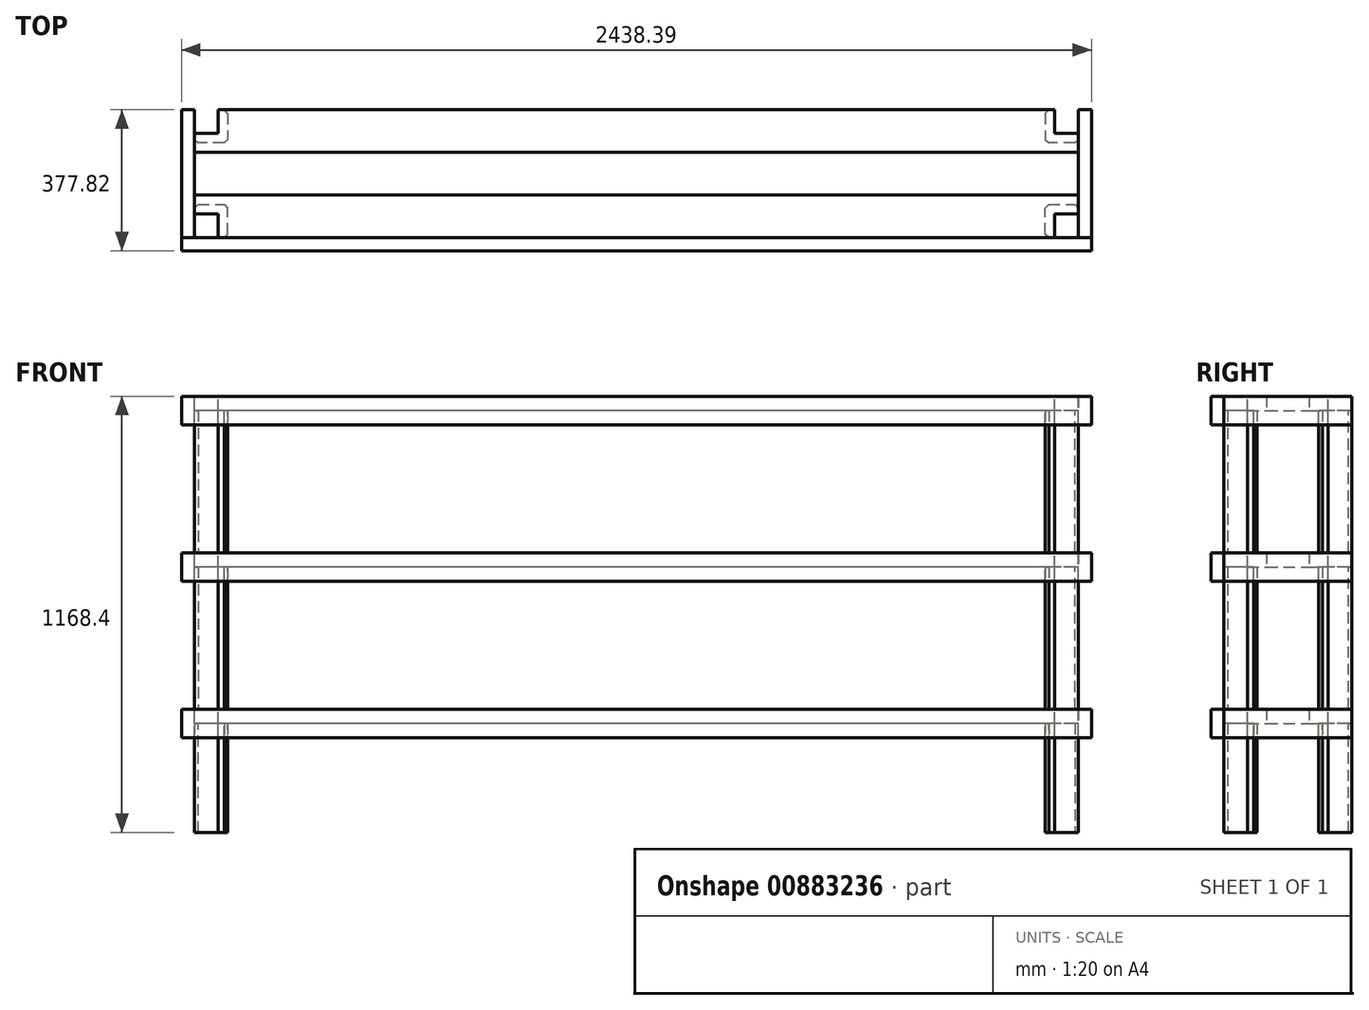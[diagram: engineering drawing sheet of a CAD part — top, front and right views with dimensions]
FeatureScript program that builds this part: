
annotation { "Feature Type Name" : "Feature", "Feature Type Description" : "" }
export const myFeature = defineFeature(function(context is Context, id is Id, definition is map)
    precondition{}
    {
        {
            var Q0;
            Q0=qCreatedBy(makeId("Top.planeOp"),FACE);
            var sketch = newSketch(context, id + "F0", { "sketchPlane" : qUnion([Q0])});
            skLineSegment(sketch, "E0.bottom", {"start": v(0, 0) * mm, "end": v(88.9, 0) * mm});
            skLineSegment(sketch, "E0.top", {"start": v(0, 88.9) * mm, "end": v(88.9, 88.9) * mm});
            skLineSegment(sketch, "E0.left", {"start": v(0, 0) * mm, "end": v(0, 88.9) * mm});
            skLineSegment(sketch, "E0.right", {"start": v(88.9, 0) * mm, "end": v(88.9, 88.9) * mm});
            skLineSegment(sketch, "E1.bottom", {"start": v(2279.65, 0) * mm, "end": v(2368.55, 0) * mm});
            skLineSegment(sketch, "E1.top", {"start": v(2279.65, 88.9) * mm, "end": v(2368.55, 88.9) * mm});
            skLineSegment(sketch, "E1.left", {"start": v(2279.65, 0) * mm, "end": v(2279.65, 88.9) * mm});
            skLineSegment(sketch, "E1.right", {"start": v(2368.55, 0) * mm, "end": v(2368.55, 88.9) * mm});
            skLineSegment(sketch, "E2.bottom", {"start": v(0, 254) * mm, "end": v(88.9, 254) * mm});
            skLineSegment(sketch, "E2.top", {"start": v(0, 342.9) * mm, "end": v(88.9, 342.9) * mm});
            skLineSegment(sketch, "E2.left", {"start": v(0, 254) * mm, "end": v(0, 342.9) * mm});
            skLineSegment(sketch, "E2.right", {"start": v(88.9, 254) * mm, "end": v(88.9, 342.9) * mm});
            skLineSegment(sketch, "E3.bottom", {"start": v(2279.65, 254) * mm, "end": v(2368.55, 254) * mm});
            skLineSegment(sketch, "E3.top", {"start": v(2279.65, 342.9) * mm, "end": v(2368.55, 342.9) * mm});
            skLineSegment(sketch, "E3.left", {"start": v(2279.65, 254) * mm, "end": v(2279.65, 342.9) * mm});
            skLineSegment(sketch, "E3.right", {"start": v(2368.55, 254) * mm, "end": v(2368.55, 342.9) * mm});
            skSolve(sketch);
        }
        {
            var Q0;
            Q0 = qSketchRegion(id + "F0", true);
            extrude(context, id + "F1", {"entities" : qUnion([Q0]), "depth" : 1168.4 * mm, "offsetDistance" : 25.4 * mm});
        }
        {
            var Q0;
            Q0=makeQuery(id+"F1.opExtrude","SWEPT_FACE",FACE,{"disambiguationData":[OSD([sQuery(id+"F0.wireOp",EDGE,"E2.left")])]});
            var sketch = newSketch(context, id + "F2", { "sketchPlane" : qUnion([Q0])});
            skLineSegment(sketch, "E4.bottom", {"start": v(-342.9, 292.1) * mm, "end": v(-228.6, 292.1) * mm});
            skLineSegment(sketch, "E4.top", {"start": v(-342.9, 330.2) * mm, "end": v(-228.6, 330.2) * mm});
            skLineSegment(sketch, "E4.left", {"start": v(-342.9, 292.1) * mm, "end": v(-342.9, 330.2) * mm});
            skLineSegment(sketch, "E4.right", {"start": v(-228.6, 292.1) * mm, "end": v(-228.6, 330.2) * mm});
            skLineSegment(sketch, "E5.bottom", {"start": v(-228.6, 292.1) * mm, "end": v(-114.3, 292.1) * mm});
            skLineSegment(sketch, "E5.top", {"start": v(-228.6, 330.2) * mm, "end": v(-114.3, 330.2) * mm});
            skLineSegment(sketch, "E5.right", {"start": v(-114.3, 292.1) * mm, "end": v(-114.3, 330.2) * mm});
            skLineSegment(sketch, "E6.bottom", {"start": v(-114.3, 292.1) * mm, "end": v(0, 292.1) * mm});
            skLineSegment(sketch, "E6.top", {"start": v(-114.3, 330.2) * mm, "end": v(0, 330.2) * mm});
            skLineSegment(sketch, "E6.right", {"start": v(0, 292.1) * mm, "end": v(0, 330.2) * mm});
            skLineSegment(sketch, "E7.bottom", {"start": v(-342.9, 711.2) * mm, "end": v(-228.6, 711.2) * mm});
            skLineSegment(sketch, "E7.top", {"start": v(-342.9, 749.3) * mm, "end": v(-228.6, 749.3) * mm});
            skLineSegment(sketch, "E7.left", {"start": v(-342.9, 711.2) * mm, "end": v(-342.9, 749.3) * mm});
            skLineSegment(sketch, "E7.right", {"start": v(-228.6, 711.2) * mm, "end": v(-228.6, 749.3) * mm});
            skLineSegment(sketch, "E8.bottom", {"start": v(-228.6, 711.2) * mm, "end": v(-114.3, 711.2) * mm});
            skLineSegment(sketch, "E8.top", {"start": v(-228.6, 749.3) * mm, "end": v(-114.3, 749.3) * mm});
            skLineSegment(sketch, "E8.right", {"start": v(-114.3, 711.2) * mm, "end": v(-114.3, 749.3) * mm});
            skLineSegment(sketch, "E9.bottom", {"start": v(-114.3, 711.2) * mm, "end": v(0, 711.2) * mm});
            skLineSegment(sketch, "E9.top", {"start": v(-114.3, 749.3) * mm, "end": v(0, 749.3) * mm});
            skLineSegment(sketch, "E9.right", {"start": v(0, 711.2) * mm, "end": v(0, 749.3) * mm});
            skLineSegment(sketch, "E10.bottom", {"start": v(-342.9, 1130.3) * mm, "end": v(-228.6, 1130.3) * mm});
            skLineSegment(sketch, "E10.top", {"start": v(-342.9, 1168.4) * mm, "end": v(-228.6, 1168.4) * mm});
            skLineSegment(sketch, "E10.left", {"start": v(-342.9, 1130.3) * mm, "end": v(-342.9, 1168.4) * mm});
            skLineSegment(sketch, "E10.right", {"start": v(-228.6, 1130.3) * mm, "end": v(-228.6, 1168.4) * mm});
            skLineSegment(sketch, "E11.bottom", {"start": v(-228.6, 1130.3) * mm, "end": v(-114.3, 1130.3) * mm});
            skLineSegment(sketch, "E11.top", {"start": v(-228.6, 1168.4) * mm, "end": v(-114.3, 1168.4) * mm});
            skLineSegment(sketch, "E11.right", {"start": v(-114.3, 1130.3) * mm, "end": v(-114.3, 1168.4) * mm});
            skLineSegment(sketch, "E12.bottom", {"start": v(-114.3, 1130.3) * mm, "end": v(0, 1130.3) * mm});
            skLineSegment(sketch, "E12.top", {"start": v(-114.3, 1168.4) * mm, "end": v(0, 1168.4) * mm});
            skLineSegment(sketch, "E12.right", {"start": v(0, 1130.3) * mm, "end": v(0, 1168.4) * mm});
            skLineSegment(sketch, "E13", {"start": v(0, 711.2) * mm, "end": v(0, 330.2) * mm, "construction": true});
            skLineSegment(sketch, "E14", {"start": v(0, 749.3) * mm, "end": v(0, 1130.3) * mm, "construction": true});
            skLineSegment(sketch, "E15.bottom", {"start": v(0, 749.3) * mm, "end": v(34.92, 749.3) * mm, "construction": true});
            skLineSegment(sketch, "E15.top", {"start": v(0, 673.1) * mm, "end": v(34.92, 673.1) * mm, "construction": true});
            skLineSegment(sketch, "E15.left", {"start": v(0, 749.3) * mm, "end": v(0, 673.1) * mm, "construction": true});
            skLineSegment(sketch, "E15.right", {"start": v(34.92, 749.3) * mm, "end": v(34.92, 673.1) * mm, "construction": true});
            skSolve(sketch);
        }
        {
            var Q0;
            {var subQ0=sQuery(id+"F2.wireOp",EDGE,"E10.right");Q0=makeQuery(id+"F2.imprint","IMPRINT",FACE,{"disambiguationData":[TD([[makeQuery(id+"F2.imprint","IMPRINT",EDGE,{"derivedFrom":subQ0}),1.0]])]});}
            var Q1;
            {var subQ0=sQuery(id+"F2.wireOp",EDGE,"E10.left");Q1=makeQuery(id+"F2.imprint","IMPRINT",FACE,{"disambiguationData":[TD([[makeQuery(id+"F2.imprint","IMPRINT",EDGE,{"derivedFrom":subQ0}),1.0]])]});}
            var Q2;
            Q2=makeQuery(id+"F2.imprint","IMPRINT",FACE,{"disambiguationData":[TD([[makeQuery(id+"F2.imprint","IMPRINT",EDGE,{"derivedFrom":sQuery(id+"F2.wireOp",EDGE,"E12.bottom")}),1.0]])]});
            var Q3;
            {var subQ0=sQuery(id+"F2.wireOp",EDGE,"E7.left");Q3=makeQuery(id+"F2.imprint","IMPRINT",FACE,{"disambiguationData":[TD([[makeQuery(id+"F2.imprint","IMPRINT",EDGE,{"derivedFrom":subQ0}),1.0]])]});}
            var Q4;
            {var subQ0=sQuery(id+"F2.wireOp",EDGE,"E7.right");Q4=makeQuery(id+"F2.imprint","IMPRINT",FACE,{"disambiguationData":[TD([[makeQuery(id+"F2.imprint","IMPRINT",EDGE,{"derivedFrom":subQ0}),1.0]])]});}
            var Q5;
            {var subQ0=sQuery(id+"F2.wireOp",EDGE,"E4.left");Q5=makeQuery(id+"F2.imprint","IMPRINT",FACE,{"disambiguationData":[TD([[makeQuery(id+"F2.imprint","IMPRINT",EDGE,{"derivedFrom":subQ0}),1.0]])]});}
            var Q6;
            {var subQ0=sQuery(id+"F2.wireOp",EDGE,"E4.right");Q6=makeQuery(id+"F2.imprint","IMPRINT",FACE,{"disambiguationData":[TD([[makeQuery(id+"F2.imprint","IMPRINT",EDGE,{"derivedFrom":subQ0}),1.0]])]});}
            var Q7;
            Q7=makeQuery(id+"F2.imprint","IMPRINT",FACE,{"disambiguationData":[TD([[makeQuery(id+"F2.imprint","IMPRINT",EDGE,{"derivedFrom":sQuery(id+"F2.wireOp",EDGE,"E6.bottom")}),1.0]])]});
            var Q8;
            Q8=makeQuery(id+"F2.imprint","IMPRINT",FACE,{"disambiguationData":[TD([[makeQuery(id+"F2.imprint","IMPRINT",EDGE,{"derivedFrom":sQuery(id+"F2.wireOp",EDGE,"E9.bottom")}),1.0]])]});
            var Q9;
            Q9=makeQuery(id+"F1.opExtrude","SWEPT_FACE",FACE,{"disambiguationData":[OSD([sQuery(id+"F0.wireOp",EDGE,"E1.right")])]});
            extrude(context, id + "F3", {"entities" : qUnion([Q0, Q1, Q2, Q3, Q4, Q5, Q6, Q7, Q8]), "endBound" : BoundingType.UP_TO_SURFACE, "oppositeDirection" : true, "depth" : 25.4 * mm, "endBoundEntityFace" : qUnion([Q9]), "offsetDistance" : 25.4 * mm});
        }
        {
            var Q0;
            Q0=makeQuery(id+"F2.imprint","IMPRINT",FACE,{"disambiguationData":[TD([[makeQuery(id+"F2.imprint","IMPRINT",EDGE,{"derivedFrom":sQuery(id+"F2.wireOp",EDGE,"E11.bottom")}),1.0]])]});
            var Q1;
            Q1=makeQuery(id+"F2.imprint","IMPRINT",FACE,{"disambiguationData":[TD([[makeQuery(id+"F2.imprint","IMPRINT",EDGE,{"derivedFrom":sQuery(id+"F2.wireOp",EDGE,"E8.bottom")}),1.0]])]});
            var Q2;
            Q2=makeQuery(id+"F2.imprint","IMPRINT",FACE,{"disambiguationData":[TD([[makeQuery(id+"F2.imprint","IMPRINT",EDGE,{"derivedFrom":sQuery(id+"F2.wireOp",EDGE,"E5.bottom")}),1.0]])]});
            var Q3;
            Q3=makeQuery(id+"F3.opExtrude","CAP_FACE",FACE,{"disambiguationData":[OSD([sQuery(id+"F2.wireOp",EDGE,"E7.bottom"),sQuery(id+"F2.wireOp",EDGE,"E7.top"),sQuery(id+"F2.wireOp",EDGE,"E7.left"),sQuery(id+"F2.wireOp",EDGE,"E7.right")])],"isStart":false});
            extrude(context, id + "F4", {"entities" : qUnion([Q0, Q1, Q2]), "endBound" : BoundingType.UP_TO_SURFACE, "oppositeDirection" : true, "depth" : 25.4 * mm, "endBoundEntityFace" : qUnion([Q3]), "offsetDistance" : 25.4 * mm});
        }
        {
            var Q0;
            Q0=makeQuery(id+"F3.opExtrude","SWEPT_FACE",FACE,{"disambiguationData":[OSD([sQuery(id+"F2.wireOp",EDGE,"E12.top")])]});
            var sketch = newSketch(context, id + "F5", { "sketchPlane" : qUnion([Q0])});
            skLineSegment(sketch, "E16.bottom", {"start": v(0, 0) * mm, "end": v(63.5, 0) * mm});
            skLineSegment(sketch, "E16.top", {"start": v(0, 63.5) * mm, "end": v(63.5, 63.5) * mm});
            skLineSegment(sketch, "E16.left", {"start": v(0, 0) * mm, "end": v(0, 63.5) * mm});
            skLineSegment(sketch, "E16.right", {"start": v(63.5, 0) * mm, "end": v(63.5, 63.5) * mm});
            skLineSegment(sketch, "E17.bottom", {"start": v(2305.05, 0) * mm, "end": v(2368.55, 0) * mm});
            skLineSegment(sketch, "E17.top", {"start": v(2305.05, 63.5) * mm, "end": v(2368.55, 63.5) * mm});
            skLineSegment(sketch, "E17.left", {"start": v(2305.05, 0) * mm, "end": v(2305.05, 63.5) * mm});
            skLineSegment(sketch, "E17.right", {"start": v(2368.55, 0) * mm, "end": v(2368.55, 63.5) * mm});
            skLineSegment(sketch, "E18.bottom", {"start": v(2305.05, 279.4) * mm, "end": v(2368.55, 279.4) * mm});
            skLineSegment(sketch, "E18.top", {"start": v(2305.05, 342.9) * mm, "end": v(2368.55, 342.9) * mm});
            skLineSegment(sketch, "E18.left", {"start": v(2305.05, 279.4) * mm, "end": v(2305.05, 342.9) * mm});
            skLineSegment(sketch, "E18.right", {"start": v(2368.55, 279.4) * mm, "end": v(2368.55, 342.9) * mm});
            skLineSegment(sketch, "E19.bottom", {"start": v(0, 279.4) * mm, "end": v(63.5, 279.4) * mm});
            skLineSegment(sketch, "E19.top", {"start": v(0, 342.9) * mm, "end": v(63.5, 342.9) * mm});
            skLineSegment(sketch, "E19.left", {"start": v(0, 279.4) * mm, "end": v(0, 342.9) * mm});
            skLineSegment(sketch, "E19.right", {"start": v(63.5, 279.4) * mm, "end": v(63.5, 342.9) * mm});
            skSolve(sketch);
        }
        {
            var Q0;
            Q0 = qSketchRegion(id + "F5", true);
            extrude(context, id + "F6", {"entities" : qUnion([Q0]), "operationType" : NewBodyOperationType.REMOVE, "endBound" : BoundingType.THROUGH_ALL, "oppositeDirection" : true, "depth" : 25.4 * mm, "offsetDistance" : 25.4 * mm});
        }
        {
            var Q0;
            Q0=makeQuery(id+"F3.opExtrude","SWEPT_BODY",BODY,{"disambiguationData":[OSD([sQuery(id+"F2.wireOp",EDGE,"E7.bottom"),sQuery(id+"F2.wireOp",EDGE,"E7.top"),sQuery(id+"F2.wireOp",EDGE,"E7.left"),sQuery(id+"F2.wireOp",EDGE,"E7.right")])]});
            var Q1;
            Q1=makeQuery(id+"F3.opExtrude","SWEPT_BODY",BODY,{"disambiguationData":[OSD([sQuery(id+"F2.wireOp",EDGE,"E9.bottom"),sQuery(id+"F2.wireOp",EDGE,"E9.top"),sQuery(id+"F2.wireOp",EDGE,"E8.right"),sQuery(id+"F2.wireOp",EDGE,"E9.right")])]});
            var Q2;
            Q2=makeQuery(id+"F3.opExtrude","SWEPT_BODY",BODY,{"disambiguationData":[OSD([sQuery(id+"F2.wireOp",EDGE,"E4.bottom"),sQuery(id+"F2.wireOp",EDGE,"E4.top"),sQuery(id+"F2.wireOp",EDGE,"E4.left"),sQuery(id+"F2.wireOp",EDGE,"E4.right")])]});
            var Q3;
            Q3=makeQuery(id+"F3.opExtrude","SWEPT_BODY",BODY,{"disambiguationData":[OSD([sQuery(id+"F2.wireOp",EDGE,"E6.bottom"),sQuery(id+"F2.wireOp",EDGE,"E6.top"),sQuery(id+"F2.wireOp",EDGE,"E5.right"),sQuery(id+"F2.wireOp",EDGE,"E6.right")])]});
            var Q4;
            Q4=makeQuery(id+"F3.opExtrude","SWEPT_BODY",BODY,{"disambiguationData":[OSD([sQuery(id+"F2.wireOp",EDGE,"E10.bottom"),sQuery(id+"F2.wireOp",EDGE,"E10.top"),sQuery(id+"F2.wireOp",EDGE,"E10.left"),sQuery(id+"F2.wireOp",EDGE,"E10.right")])]});
            var Q5;
            Q5=makeQuery(id+"F3.opExtrude","SWEPT_BODY",BODY,{"disambiguationData":[OSD([sQuery(id+"F2.wireOp",EDGE,"E12.bottom"),sQuery(id+"F2.wireOp",EDGE,"E12.top"),sQuery(id+"F2.wireOp",EDGE,"E11.right"),sQuery(id+"F2.wireOp",EDGE,"E12.right")])]});
            var Q6;
            Q6=makeQuery(id+"F1.opExtrude","SWEPT_BODY",BODY,{"disambiguationData":[OSD([sQuery(id+"F0.wireOp",EDGE,"E2.bottom"),sQuery(id+"F0.wireOp",EDGE,"E2.top"),sQuery(id+"F0.wireOp",EDGE,"E2.left"),sQuery(id+"F0.wireOp",EDGE,"E2.right")])]});
            var Q7;
            Q7=makeQuery(id+"F1.opExtrude","SWEPT_BODY",BODY,{"disambiguationData":[OSD([sQuery(id+"F0.wireOp",EDGE,"E0.bottom"),sQuery(id+"F0.wireOp",EDGE,"E0.top"),sQuery(id+"F0.wireOp",EDGE,"E0.left"),sQuery(id+"F0.wireOp",EDGE,"E0.right")])]});
            var Q8;
            Q8=makeQuery(id+"F1.opExtrude","SWEPT_BODY",BODY,{"disambiguationData":[OSD([sQuery(id+"F0.wireOp",EDGE,"E3.bottom"),sQuery(id+"F0.wireOp",EDGE,"E3.top"),sQuery(id+"F0.wireOp",EDGE,"E3.left"),sQuery(id+"F0.wireOp",EDGE,"E3.right")])]});
            var Q9;
            Q9=makeQuery(id+"F1.opExtrude","SWEPT_BODY",BODY,{"disambiguationData":[OSD([sQuery(id+"F0.wireOp",EDGE,"E1.bottom"),sQuery(id+"F0.wireOp",EDGE,"E1.top"),sQuery(id+"F0.wireOp",EDGE,"E1.left"),sQuery(id+"F0.wireOp",EDGE,"E1.right")])]});
            booleanBodies(context, id + "F7", {"operationType" : BooleanOperationType.SUBTRACTION, "tools" : qUnion([Q0, Q1, Q2, Q3, Q4, Q5]), "targets" : qUnion([Q6, Q7, Q8, Q9]), "keepTools" : true});
        }
        {
            var Q0;
            Q0=makeQuery(id+"F1.opExtrude","SWEPT_FACE",FACE,{"disambiguationData":[OSD([sQuery(id+"F0.wireOp",EDGE,"E3.top")])]});
            var sketch = newSketch(context, id + "F8", { "sketchPlane" : qUnion([Q0])});
            skLineSegment(sketch, "E20.bottom", {"start": v(-2368.55, 1168.4) * mm, "end": v(-2403.47, 1168.4) * mm});
            skLineSegment(sketch, "E20.top", {"start": v(-2368.55, 1092.2) * mm, "end": v(-2403.47, 1092.2) * mm});
            skLineSegment(sketch, "E20.left", {"start": v(-2368.55, 1168.4) * mm, "end": v(-2368.55, 1092.2) * mm});
            skLineSegment(sketch, "E20.right", {"start": v(-2403.47, 1168.4) * mm, "end": v(-2403.47, 1092.2) * mm});
            skLineSegment(sketch, "E21.bottom", {"start": v(-2368.55, 749.3) * mm, "end": v(-2403.47, 749.3) * mm});
            skLineSegment(sketch, "E21.top", {"start": v(-2368.55, 673.1) * mm, "end": v(-2403.47, 673.1) * mm});
            skLineSegment(sketch, "E21.left", {"start": v(-2368.55, 749.3) * mm, "end": v(-2368.55, 673.1) * mm});
            skLineSegment(sketch, "E21.right", {"start": v(-2403.47, 749.3) * mm, "end": v(-2403.47, 673.1) * mm});
            skLineSegment(sketch, "E22.bottom", {"start": v(-2368.55, 330.2) * mm, "end": v(-2403.47, 330.2) * mm});
            skLineSegment(sketch, "E22.top", {"start": v(-2368.55, 254) * mm, "end": v(-2403.47, 254) * mm});
            skLineSegment(sketch, "E22.left", {"start": v(-2368.55, 330.2) * mm, "end": v(-2368.55, 254) * mm});
            skLineSegment(sketch, "E22.right", {"start": v(-2403.47, 330.2) * mm, "end": v(-2403.47, 254) * mm});
            skLineSegment(sketch, "E23.bottom", {"start": v(0, 1168.4) * mm, "end": v(34.92, 1168.4) * mm});
            skLineSegment(sketch, "E23.top", {"start": v(0, 1092.2) * mm, "end": v(34.92, 1092.2) * mm});
            skLineSegment(sketch, "E23.left", {"start": v(0, 1168.4) * mm, "end": v(0, 1092.2) * mm});
            skLineSegment(sketch, "E23.right", {"start": v(34.92, 1168.4) * mm, "end": v(34.92, 1092.2) * mm});
            skLineSegment(sketch, "E24.bottom", {"start": v(0, 749.3) * mm, "end": v(34.92, 749.3) * mm});
            skLineSegment(sketch, "E24.top", {"start": v(0, 673.1) * mm, "end": v(34.92, 673.1) * mm});
            skLineSegment(sketch, "E24.left", {"start": v(0, 749.3) * mm, "end": v(0, 673.1) * mm});
            skLineSegment(sketch, "E24.right", {"start": v(34.92, 749.3) * mm, "end": v(34.92, 673.1) * mm});
            skLineSegment(sketch, "E25.bottom", {"start": v(0, 330.2) * mm, "end": v(34.92, 330.2) * mm});
            skLineSegment(sketch, "E25.top", {"start": v(0, 254) * mm, "end": v(34.92, 254) * mm});
            skLineSegment(sketch, "E25.left", {"start": v(0, 330.2) * mm, "end": v(0, 254) * mm});
            skLineSegment(sketch, "E25.right", {"start": v(34.92, 330.2) * mm, "end": v(34.92, 254) * mm});
            skSolve(sketch);
        }
        {
            var Q0;
            Q0 = qSketchRegion(id + "F8", true);
            var Q1;
            Q1=makeQuery(id+"F1.opExtrude","SWEPT_FACE",FACE,{"disambiguationData":[OSD([sQuery(id+"F0.wireOp",EDGE,"E0.bottom")])]});
            extrude(context, id + "F9", {"entities" : qUnion([Q0]), "endBound" : BoundingType.UP_TO_SURFACE, "oppositeDirection" : true, "depth" : 25.4 * mm, "endBoundEntityFace" : qUnion([Q1]), "offsetDistance" : 25.4 * mm});
        }
        {
            var Q0;
            Q0=makeQuery(id+"F1.opExtrude","SWEPT_FACE",FACE,{"disambiguationData":[OSD([sQuery(id+"F0.wireOp",EDGE,"E0.bottom")])]});
            var sketch = newSketch(context, id + "F10", { "sketchPlane" : qUnion([Q0])});
            skLineSegment(sketch, "E26.bottom", {"start": v(-34.92, 330.2) * mm, "end": v(2403.47, 330.2) * mm});
            skLineSegment(sketch, "E26.top", {"start": v(-34.92, 254) * mm, "end": v(2403.47, 254) * mm});
            skLineSegment(sketch, "E26.left", {"start": v(-34.92, 330.2) * mm, "end": v(-34.92, 254) * mm});
            skLineSegment(sketch, "E26.right", {"start": v(2403.47, 330.2) * mm, "end": v(2403.47, 254) * mm});
            skLineSegment(sketch, "E27.bottom", {"start": v(-34.92, 749.3) * mm, "end": v(2403.47, 749.3) * mm});
            skLineSegment(sketch, "E27.top", {"start": v(-34.92, 673.1) * mm, "end": v(2403.47, 673.1) * mm});
            skLineSegment(sketch, "E27.left", {"start": v(-34.92, 749.3) * mm, "end": v(-34.92, 673.1) * mm});
            skLineSegment(sketch, "E27.right", {"start": v(2403.47, 749.3) * mm, "end": v(2403.47, 673.1) * mm});
            skLineSegment(sketch, "E28.bottom", {"start": v(-34.92, 1168.4) * mm, "end": v(2403.47, 1168.4) * mm});
            skLineSegment(sketch, "E28.top", {"start": v(-34.92, 1092.2) * mm, "end": v(2403.47, 1092.2) * mm});
            skLineSegment(sketch, "E28.left", {"start": v(-34.92, 1168.4) * mm, "end": v(-34.92, 1092.2) * mm});
            skLineSegment(sketch, "E28.right", {"start": v(2403.47, 1168.4) * mm, "end": v(2403.47, 1092.2) * mm});
            skSolve(sketch);
        }
        {
            var Q0;
            Q0 = qSketchRegion(id + "F10", true);
            extrude(context, id + "F11", {"entities" : qUnion([Q0]), "depth" : 34.92 * mm, "offsetDistance" : 25.4 * mm});
        }
        {
            var Q0;
            Q0=makeQuery(id+"F1.opExtrude","SWEPT_EDGE",EDGE,{"disambiguationData":[OSD([sQuery(id+"F0.wireOp",EDGE,"E0.bottom"),sQuery(id+"F0.wireOp",EDGE,"E0.left")])]});
            var Q1;
            {var subQ0=sQuery(id+"F0.wireOp",EDGE,"E0.bottom");var subQ1=sQuery(id+"F0.wireOp",EDGE,"E0.right");Q1=makeQuery(id+"F7.opBoolean","SPLIT",EDGE,{"disambiguationData":[TD([makeQuery(id+"F3.opExtrude","SWEPT_FACE",FACE,{"disambiguationData":[OSD([sQuery(id+"F2.wireOp",EDGE,"E9.top")])]})])],"derivedFrom":makeQuery(id+"F1.opExtrude","SWEPT_EDGE",EDGE,{"disambiguationData":[OSD([subQ0,subQ1])]})});}
            var Q2;
            {var subQ0=sQuery(id+"F0.wireOp",EDGE,"E0.bottom");var subQ1=sQuery(id+"F0.wireOp",EDGE,"E0.right");Q2=makeQuery(id+"F7.opBoolean","SPLIT",EDGE,{"disambiguationData":[TD([makeQuery(id+"F3.opExtrude","SWEPT_FACE",FACE,{"disambiguationData":[OSD([sQuery(id+"F2.wireOp",EDGE,"E6.top")])]})])],"derivedFrom":makeQuery(id+"F1.opExtrude","SWEPT_EDGE",EDGE,{"disambiguationData":[OSD([subQ0,subQ1])]})});}
            var Q3;
            {var subQ0=sQuery(id+"F0.wireOp",EDGE,"E0.bottom");var subQ1=sQuery(id+"F0.wireOp",EDGE,"E0.right");Q3=makeQuery(id+"F7.opBoolean","SPLIT",EDGE,{"disambiguationData":[TD([makeQuery(id+"F3.opExtrude","SWEPT_FACE",FACE,{"disambiguationData":[OSD([sQuery(id+"F2.wireOp",EDGE,"E6.bottom")])]})])],"derivedFrom":makeQuery(id+"F1.opExtrude","SWEPT_EDGE",EDGE,{"disambiguationData":[OSD([subQ0,subQ1])]})});}
            var Q4;
            {var subQ0=sQuery(id+"F0.wireOp",EDGE,"E0.right");var subQ1=sQuery(id+"F0.wireOp",EDGE,"E0.top");Q4=makeQuery(id+"F7.opBoolean","SPLIT",EDGE,{"disambiguationData":[TD([makeQuery(id+"F3.opExtrude","SWEPT_FACE",FACE,{"disambiguationData":[OSD([sQuery(id+"F2.wireOp",EDGE,"E6.bottom")])]})])],"derivedFrom":makeQuery(id+"F1.opExtrude","SWEPT_EDGE",EDGE,{"disambiguationData":[OSD([subQ1,subQ0])]})});}
            var Q5;
            {var subQ0=sQuery(id+"F0.wireOp",EDGE,"E0.top");var subQ1=sQuery(id+"F0.wireOp",EDGE,"E0.left");Q5=makeQuery(id+"F7.opBoolean","SPLIT",EDGE,{"disambiguationData":[TD([makeQuery(id+"F3.opExtrude","SWEPT_FACE",FACE,{"disambiguationData":[OSD([sQuery(id+"F2.wireOp",EDGE,"E9.top")])]})])],"derivedFrom":makeQuery(id+"F1.opExtrude","SWEPT_EDGE",EDGE,{"disambiguationData":[OSD([subQ0,subQ1])]})});}
            var Q6;
            {var subQ0=sQuery(id+"F0.wireOp",EDGE,"E0.top");var subQ1=sQuery(id+"F0.wireOp",EDGE,"E0.left");Q6=makeQuery(id+"F7.opBoolean","SPLIT",EDGE,{"disambiguationData":[TD([makeQuery(id+"F3.opExtrude","SWEPT_FACE",FACE,{"disambiguationData":[OSD([sQuery(id+"F2.wireOp",EDGE,"E6.top")])]})])],"derivedFrom":makeQuery(id+"F1.opExtrude","SWEPT_EDGE",EDGE,{"disambiguationData":[OSD([subQ0,subQ1])]})});}
            var Q7;
            {var subQ0=sQuery(id+"F0.wireOp",EDGE,"E0.left");var subQ1=sQuery(id+"F0.wireOp",EDGE,"E0.top");Q7=makeQuery(id+"F7.opBoolean","SPLIT",EDGE,{"disambiguationData":[TD([makeQuery(id+"F3.opExtrude","SWEPT_FACE",FACE,{"disambiguationData":[OSD([sQuery(id+"F2.wireOp",EDGE,"E6.bottom")])]})])],"derivedFrom":makeQuery(id+"F1.opExtrude","SWEPT_EDGE",EDGE,{"disambiguationData":[OSD([subQ1,subQ0])]})});}
            var Q8;
            {var subQ0=sQuery(id+"F0.wireOp",EDGE,"E0.top");var subQ1=sQuery(id+"F0.wireOp",EDGE,"E0.right");Q8=makeQuery(id+"F7.opBoolean","SPLIT",EDGE,{"disambiguationData":[TD([makeQuery(id+"F3.opExtrude","SWEPT_FACE",FACE,{"disambiguationData":[OSD([sQuery(id+"F2.wireOp",EDGE,"E9.top")])]})])],"derivedFrom":makeQuery(id+"F1.opExtrude","SWEPT_EDGE",EDGE,{"disambiguationData":[OSD([subQ0,subQ1])]})});}
            var Q9;
            {var subQ0=sQuery(id+"F0.wireOp",EDGE,"E0.top");var subQ1=sQuery(id+"F0.wireOp",EDGE,"E0.right");Q9=makeQuery(id+"F7.opBoolean","SPLIT",EDGE,{"disambiguationData":[TD([makeQuery(id+"F3.opExtrude","SWEPT_FACE",FACE,{"disambiguationData":[OSD([sQuery(id+"F2.wireOp",EDGE,"E6.top")])]})])],"derivedFrom":makeQuery(id+"F1.opExtrude","SWEPT_EDGE",EDGE,{"disambiguationData":[OSD([subQ0,subQ1])]})});}
            var Q10;
            {var subQ0=sQuery(id+"F0.wireOp",EDGE,"E2.top");var subQ1=sQuery(id+"F0.wireOp",EDGE,"E2.right");Q10=makeQuery(id+"F7.opBoolean","SPLIT",EDGE,{"disambiguationData":[TD([makeQuery(id+"F3.opExtrude","SWEPT_FACE",FACE,{"disambiguationData":[OSD([sQuery(id+"F2.wireOp",EDGE,"E7.top")])]})])],"derivedFrom":makeQuery(id+"F1.opExtrude","SWEPT_EDGE",EDGE,{"disambiguationData":[OSD([subQ0,subQ1])]})});}
            var Q11;
            {var subQ0=sQuery(id+"F0.wireOp",EDGE,"E2.top");var subQ1=sQuery(id+"F0.wireOp",EDGE,"E2.right");Q11=makeQuery(id+"F7.opBoolean","SPLIT",EDGE,{"disambiguationData":[TD([makeQuery(id+"F3.opExtrude","SWEPT_FACE",FACE,{"disambiguationData":[OSD([sQuery(id+"F2.wireOp",EDGE,"E4.top")])]})])],"derivedFrom":makeQuery(id+"F1.opExtrude","SWEPT_EDGE",EDGE,{"disambiguationData":[OSD([subQ0,subQ1])]})});}
            var Q12;
            {var subQ0=sQuery(id+"F0.wireOp",EDGE,"E2.right");var subQ1=sQuery(id+"F0.wireOp",EDGE,"E2.top");Q12=makeQuery(id+"F7.opBoolean","SPLIT",EDGE,{"disambiguationData":[TD([makeQuery(id+"F3.opExtrude","SWEPT_FACE",FACE,{"disambiguationData":[OSD([sQuery(id+"F2.wireOp",EDGE,"E4.bottom")])]})])],"derivedFrom":makeQuery(id+"F1.opExtrude","SWEPT_EDGE",EDGE,{"disambiguationData":[OSD([subQ1,subQ0])]})});}
            var Q13;
            {var subQ0=sQuery(id+"F0.wireOp",EDGE,"E2.bottom");var subQ1=sQuery(id+"F0.wireOp",EDGE,"E2.right");Q13=makeQuery(id+"F7.opBoolean","SPLIT",EDGE,{"disambiguationData":[TD([makeQuery(id+"F3.opExtrude","SWEPT_FACE",FACE,{"disambiguationData":[OSD([sQuery(id+"F2.wireOp",EDGE,"E4.bottom")])]})])],"derivedFrom":makeQuery(id+"F1.opExtrude","SWEPT_EDGE",EDGE,{"disambiguationData":[OSD([subQ0,subQ1])]})});}
            var Q14;
            {var subQ0=sQuery(id+"F0.wireOp",EDGE,"E2.bottom");var subQ1=sQuery(id+"F0.wireOp",EDGE,"E2.right");Q14=makeQuery(id+"F7.opBoolean","SPLIT",EDGE,{"disambiguationData":[TD([makeQuery(id+"F3.opExtrude","SWEPT_FACE",FACE,{"disambiguationData":[OSD([sQuery(id+"F2.wireOp",EDGE,"E4.top")])]})])],"derivedFrom":makeQuery(id+"F1.opExtrude","SWEPT_EDGE",EDGE,{"disambiguationData":[OSD([subQ0,subQ1])]})});}
            var Q15;
            {var subQ0=sQuery(id+"F0.wireOp",EDGE,"E2.bottom");var subQ1=sQuery(id+"F0.wireOp",EDGE,"E2.right");Q15=makeQuery(id+"F7.opBoolean","SPLIT",EDGE,{"disambiguationData":[TD([makeQuery(id+"F3.opExtrude","SWEPT_FACE",FACE,{"disambiguationData":[OSD([sQuery(id+"F2.wireOp",EDGE,"E7.top")])]})])],"derivedFrom":makeQuery(id+"F1.opExtrude","SWEPT_EDGE",EDGE,{"disambiguationData":[OSD([subQ0,subQ1])]})});}
            var Q16;
            {var subQ0=sQuery(id+"F0.wireOp",EDGE,"E2.bottom");var subQ1=sQuery(id+"F0.wireOp",EDGE,"E2.left");Q16=makeQuery(id+"F7.opBoolean","SPLIT",EDGE,{"disambiguationData":[TD([makeQuery(id+"F3.opExtrude","SWEPT_FACE",FACE,{"disambiguationData":[OSD([sQuery(id+"F2.wireOp",EDGE,"E7.top")])]})])],"derivedFrom":makeQuery(id+"F1.opExtrude","SWEPT_EDGE",EDGE,{"disambiguationData":[OSD([subQ0,subQ1])]})});}
            var Q17;
            {var subQ0=sQuery(id+"F0.wireOp",EDGE,"E2.bottom");var subQ1=sQuery(id+"F0.wireOp",EDGE,"E2.left");Q17=makeQuery(id+"F7.opBoolean","SPLIT",EDGE,{"disambiguationData":[TD([makeQuery(id+"F3.opExtrude","SWEPT_FACE",FACE,{"disambiguationData":[OSD([sQuery(id+"F2.wireOp",EDGE,"E4.top")])]})])],"derivedFrom":makeQuery(id+"F1.opExtrude","SWEPT_EDGE",EDGE,{"disambiguationData":[OSD([subQ0,subQ1])]})});}
            var Q18;
            {var subQ0=sQuery(id+"F0.wireOp",EDGE,"E2.bottom");var subQ1=sQuery(id+"F0.wireOp",EDGE,"E2.left");Q18=makeQuery(id+"F7.opBoolean","SPLIT",EDGE,{"disambiguationData":[TD([makeQuery(id+"F3.opExtrude","SWEPT_FACE",FACE,{"disambiguationData":[OSD([sQuery(id+"F2.wireOp",EDGE,"E4.bottom")])]})])],"derivedFrom":makeQuery(id+"F1.opExtrude","SWEPT_EDGE",EDGE,{"disambiguationData":[OSD([subQ0,subQ1])]})});}
            var Q19;
            Q19=makeQuery(id+"F1.opExtrude","SWEPT_EDGE",EDGE,{"disambiguationData":[OSD([sQuery(id+"F0.wireOp",EDGE,"E2.top"),sQuery(id+"F0.wireOp",EDGE,"E2.left")])]});
            var Q20;
            {var subQ0=sQuery(id+"F0.wireOp",EDGE,"E3.bottom");var subQ1=sQuery(id+"F0.wireOp",EDGE,"E3.left");Q20=makeQuery(id+"F7.opBoolean","SPLIT",EDGE,{"disambiguationData":[TD([makeQuery(id+"F3.opExtrude","SWEPT_FACE",FACE,{"disambiguationData":[OSD([sQuery(id+"F2.wireOp",EDGE,"E4.bottom")])]})])],"derivedFrom":makeQuery(id+"F1.opExtrude","SWEPT_EDGE",EDGE,{"disambiguationData":[OSD([subQ0,subQ1])]})});}
            var Q21;
            {var subQ0=sQuery(id+"F0.wireOp",EDGE,"E3.bottom");var subQ1=sQuery(id+"F0.wireOp",EDGE,"E3.left");Q21=makeQuery(id+"F7.opBoolean","SPLIT",EDGE,{"disambiguationData":[TD([makeQuery(id+"F3.opExtrude","SWEPT_FACE",FACE,{"disambiguationData":[OSD([sQuery(id+"F2.wireOp",EDGE,"E4.top")])]})])],"derivedFrom":makeQuery(id+"F1.opExtrude","SWEPT_EDGE",EDGE,{"disambiguationData":[OSD([subQ0,subQ1])]})});}
            var Q22;
            {var subQ0=sQuery(id+"F0.wireOp",EDGE,"E3.bottom");var subQ1=sQuery(id+"F0.wireOp",EDGE,"E3.left");Q22=makeQuery(id+"F7.opBoolean","SPLIT",EDGE,{"disambiguationData":[TD([makeQuery(id+"F3.opExtrude","SWEPT_FACE",FACE,{"disambiguationData":[OSD([sQuery(id+"F2.wireOp",EDGE,"E7.top")])]})])],"derivedFrom":makeQuery(id+"F1.opExtrude","SWEPT_EDGE",EDGE,{"disambiguationData":[OSD([subQ0,subQ1])]})});}
            var Q23;
            {var subQ0=sQuery(id+"F0.wireOp",EDGE,"E3.top");var subQ1=sQuery(id+"F0.wireOp",EDGE,"E3.left");Q23=makeQuery(id+"F7.opBoolean","SPLIT",EDGE,{"disambiguationData":[TD([makeQuery(id+"F3.opExtrude","SWEPT_FACE",FACE,{"disambiguationData":[OSD([sQuery(id+"F2.wireOp",EDGE,"E7.top")])]})])],"derivedFrom":makeQuery(id+"F1.opExtrude","SWEPT_EDGE",EDGE,{"disambiguationData":[OSD([subQ0,subQ1])]})});}
            var Q24;
            {var subQ0=sQuery(id+"F0.wireOp",EDGE,"E3.top");var subQ1=sQuery(id+"F0.wireOp",EDGE,"E3.left");Q24=makeQuery(id+"F7.opBoolean","SPLIT",EDGE,{"disambiguationData":[TD([makeQuery(id+"F3.opExtrude","SWEPT_FACE",FACE,{"disambiguationData":[OSD([sQuery(id+"F2.wireOp",EDGE,"E4.top")])]})])],"derivedFrom":makeQuery(id+"F1.opExtrude","SWEPT_EDGE",EDGE,{"disambiguationData":[OSD([subQ0,subQ1])]})});}
            var Q25;
            {var subQ0=sQuery(id+"F0.wireOp",EDGE,"E3.left");var subQ1=sQuery(id+"F0.wireOp",EDGE,"E3.top");Q25=makeQuery(id+"F7.opBoolean","SPLIT",EDGE,{"disambiguationData":[TD([makeQuery(id+"F3.opExtrude","SWEPT_FACE",FACE,{"disambiguationData":[OSD([sQuery(id+"F2.wireOp",EDGE,"E4.bottom")])]})])],"derivedFrom":makeQuery(id+"F1.opExtrude","SWEPT_EDGE",EDGE,{"disambiguationData":[OSD([subQ1,subQ0])]})});}
            var Q26;
            Q26=makeQuery(id+"F1.opExtrude","SWEPT_EDGE",EDGE,{"disambiguationData":[OSD([sQuery(id+"F0.wireOp",EDGE,"E3.top"),sQuery(id+"F0.wireOp",EDGE,"E3.right")])]});
            var Q27;
            {var subQ0=sQuery(id+"F0.wireOp",EDGE,"E1.right");var subQ1=sQuery(id+"F0.wireOp",EDGE,"E1.top");Q27=makeQuery(id+"F7.opBoolean","SPLIT",EDGE,{"disambiguationData":[TD([makeQuery(id+"F3.opExtrude","SWEPT_FACE",FACE,{"disambiguationData":[OSD([sQuery(id+"F2.wireOp",EDGE,"E6.bottom")])]})])],"derivedFrom":makeQuery(id+"F1.opExtrude","SWEPT_EDGE",EDGE,{"disambiguationData":[OSD([subQ1,subQ0])]})});}
            var Q28;
            {var subQ0=sQuery(id+"F0.wireOp",EDGE,"E1.left");var subQ1=sQuery(id+"F0.wireOp",EDGE,"E1.top");Q28=makeQuery(id+"F7.opBoolean","SPLIT",EDGE,{"disambiguationData":[TD([makeQuery(id+"F3.opExtrude","SWEPT_FACE",FACE,{"disambiguationData":[OSD([sQuery(id+"F2.wireOp",EDGE,"E6.bottom")])]})])],"derivedFrom":makeQuery(id+"F1.opExtrude","SWEPT_EDGE",EDGE,{"disambiguationData":[OSD([subQ1,subQ0])]})});}
            var Q29;
            {var subQ0=sQuery(id+"F0.wireOp",EDGE,"E1.top");var subQ1=sQuery(id+"F0.wireOp",EDGE,"E1.right");Q29=makeQuery(id+"F7.opBoolean","SPLIT",EDGE,{"disambiguationData":[TD([makeQuery(id+"F3.opExtrude","SWEPT_FACE",FACE,{"disambiguationData":[OSD([sQuery(id+"F2.wireOp",EDGE,"E6.top")])]})])],"derivedFrom":makeQuery(id+"F1.opExtrude","SWEPT_EDGE",EDGE,{"disambiguationData":[OSD([subQ0,subQ1])]})});}
            var Q30;
            {var subQ0=sQuery(id+"F0.wireOp",EDGE,"E1.top");var subQ1=sQuery(id+"F0.wireOp",EDGE,"E1.left");Q30=makeQuery(id+"F7.opBoolean","SPLIT",EDGE,{"disambiguationData":[TD([makeQuery(id+"F3.opExtrude","SWEPT_FACE",FACE,{"disambiguationData":[OSD([sQuery(id+"F2.wireOp",EDGE,"E6.top")])]})])],"derivedFrom":makeQuery(id+"F1.opExtrude","SWEPT_EDGE",EDGE,{"disambiguationData":[OSD([subQ0,subQ1])]})});}
            var Q31;
            {var subQ0=sQuery(id+"F0.wireOp",EDGE,"E1.top");var subQ1=sQuery(id+"F0.wireOp",EDGE,"E1.right");Q31=makeQuery(id+"F7.opBoolean","SPLIT",EDGE,{"disambiguationData":[TD([makeQuery(id+"F3.opExtrude","SWEPT_FACE",FACE,{"disambiguationData":[OSD([sQuery(id+"F2.wireOp",EDGE,"E9.top")])]})])],"derivedFrom":makeQuery(id+"F1.opExtrude","SWEPT_EDGE",EDGE,{"disambiguationData":[OSD([subQ0,subQ1])]})});}
            var Q32;
            {var subQ0=sQuery(id+"F0.wireOp",EDGE,"E1.top");var subQ1=sQuery(id+"F0.wireOp",EDGE,"E1.left");Q32=makeQuery(id+"F7.opBoolean","SPLIT",EDGE,{"disambiguationData":[TD([makeQuery(id+"F3.opExtrude","SWEPT_FACE",FACE,{"disambiguationData":[OSD([sQuery(id+"F2.wireOp",EDGE,"E9.top")])]})])],"derivedFrom":makeQuery(id+"F1.opExtrude","SWEPT_EDGE",EDGE,{"disambiguationData":[OSD([subQ0,subQ1])]})});}
            var Q33;
            {var subQ0=sQuery(id+"F0.wireOp",EDGE,"E1.bottom");var subQ1=sQuery(id+"F0.wireOp",EDGE,"E1.left");Q33=makeQuery(id+"F7.opBoolean","SPLIT",EDGE,{"disambiguationData":[TD([makeQuery(id+"F3.opExtrude","SWEPT_FACE",FACE,{"disambiguationData":[OSD([sQuery(id+"F2.wireOp",EDGE,"E9.top")])]})])],"derivedFrom":makeQuery(id+"F1.opExtrude","SWEPT_EDGE",EDGE,{"disambiguationData":[OSD([subQ0,subQ1])]})});}
            var Q34;
            {var subQ0=sQuery(id+"F0.wireOp",EDGE,"E1.bottom");var subQ1=sQuery(id+"F0.wireOp",EDGE,"E1.left");Q34=makeQuery(id+"F7.opBoolean","SPLIT",EDGE,{"disambiguationData":[TD([makeQuery(id+"F3.opExtrude","SWEPT_FACE",FACE,{"disambiguationData":[OSD([sQuery(id+"F2.wireOp",EDGE,"E6.top")])]})])],"derivedFrom":makeQuery(id+"F1.opExtrude","SWEPT_EDGE",EDGE,{"disambiguationData":[OSD([subQ0,subQ1])]})});}
            var Q35;
            {var subQ0=sQuery(id+"F0.wireOp",EDGE,"E3.bottom");var subQ1=sQuery(id+"F0.wireOp",EDGE,"E3.right");Q35=makeQuery(id+"F7.opBoolean","SPLIT",EDGE,{"disambiguationData":[TD([makeQuery(id+"F3.opExtrude","SWEPT_FACE",FACE,{"disambiguationData":[OSD([sQuery(id+"F2.wireOp",EDGE,"E4.bottom")])]})])],"derivedFrom":makeQuery(id+"F1.opExtrude","SWEPT_EDGE",EDGE,{"disambiguationData":[OSD([subQ0,subQ1])]})});}
            var Q36;
            Q36=makeQuery(id+"F1.opExtrude","SWEPT_EDGE",EDGE,{"disambiguationData":[OSD([sQuery(id+"F0.wireOp",EDGE,"E1.bottom"),sQuery(id+"F0.wireOp",EDGE,"E1.right")])]});
            var Q37;
            {var subQ0=sQuery(id+"F0.wireOp",EDGE,"E1.bottom");var subQ1=sQuery(id+"F0.wireOp",EDGE,"E1.left");Q37=makeQuery(id+"F7.opBoolean","SPLIT",EDGE,{"disambiguationData":[TD([makeQuery(id+"F3.opExtrude","SWEPT_FACE",FACE,{"disambiguationData":[OSD([sQuery(id+"F2.wireOp",EDGE,"E6.bottom")])]})])],"derivedFrom":makeQuery(id+"F1.opExtrude","SWEPT_EDGE",EDGE,{"disambiguationData":[OSD([subQ0,subQ1])]})});}
            var Q38;
            {var subQ0=sQuery(id+"F0.wireOp",EDGE,"E3.bottom");var subQ1=sQuery(id+"F0.wireOp",EDGE,"E3.right");Q38=makeQuery(id+"F7.opBoolean","SPLIT",EDGE,{"disambiguationData":[TD([makeQuery(id+"F3.opExtrude","SWEPT_FACE",FACE,{"disambiguationData":[OSD([sQuery(id+"F2.wireOp",EDGE,"E7.top")])]})])],"derivedFrom":makeQuery(id+"F1.opExtrude","SWEPT_EDGE",EDGE,{"disambiguationData":[OSD([subQ0,subQ1])]})});}
            var Q39;
            {var subQ0=sQuery(id+"F0.wireOp",EDGE,"E3.bottom");var subQ1=sQuery(id+"F0.wireOp",EDGE,"E3.right");Q39=makeQuery(id+"F7.opBoolean","SPLIT",EDGE,{"disambiguationData":[TD([makeQuery(id+"F3.opExtrude","SWEPT_FACE",FACE,{"disambiguationData":[OSD([sQuery(id+"F2.wireOp",EDGE,"E4.top")])]})])],"derivedFrom":makeQuery(id+"F1.opExtrude","SWEPT_EDGE",EDGE,{"disambiguationData":[OSD([subQ0,subQ1])]})});}
            chamfer(context, id + "F12", {"entities" : qUnion([Q0, Q1, Q2, Q3, Q4, Q5, Q6, Q7, Q8, Q9, Q10, Q11, Q12, Q13, Q14, Q15, Q16, Q17, Q18, Q19, Q20, Q21, Q22, Q23, Q24, Q25, Q26, Q27, Q28, Q29, Q30, Q31, Q32, Q33, Q34, Q35, Q36, Q37, Q38, Q39]), "width" : 9.52 * mm, "tangentPropagation" : true});
        }
    });
